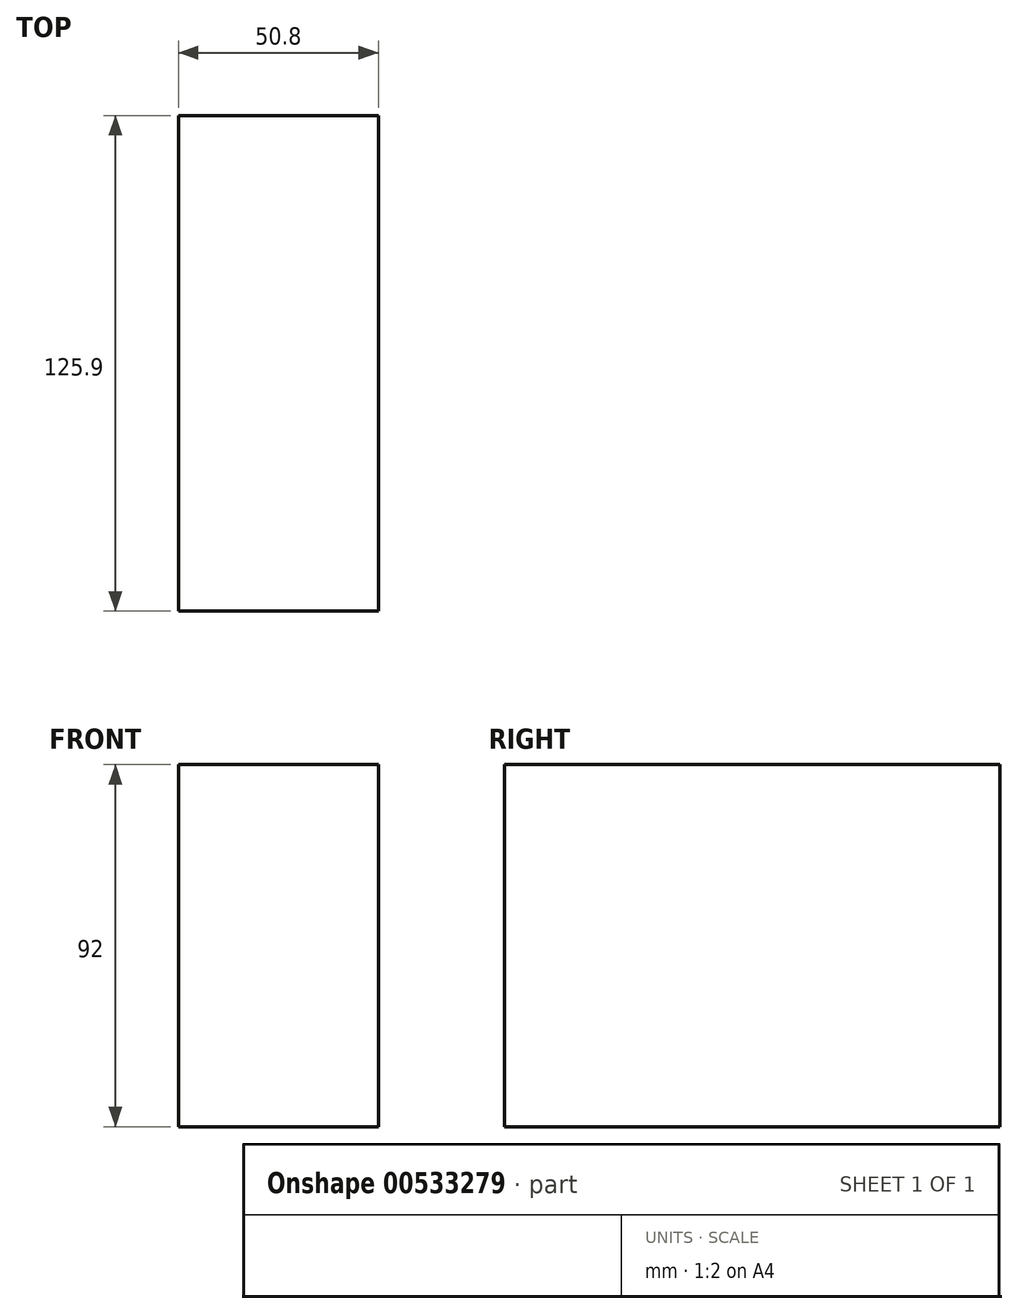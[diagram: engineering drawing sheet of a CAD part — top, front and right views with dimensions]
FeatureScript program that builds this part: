
annotation { "Feature Type Name" : "Feature", "Feature Type Description" : "" }
export const myFeature = defineFeature(function(context is Context, id is Id, definition is map)
    precondition{}
    {
        {
            var Q0;
            Q0=qCreatedBy(makeId("Right.planeOp"),FACE);
            var sketch = newSketch(context, id + "F0", { "sketchPlane" : qUnion([Q0])});
            skLineSegment(sketch, "E0.bottom", {"start": v(0, 0) * mm, "end": v(-125.9, 0) * mm});
            skLineSegment(sketch, "E0.top", {"start": v(0, -92) * mm, "end": v(-125.9, -92) * mm});
            skLineSegment(sketch, "E0.left", {"start": v(0, 0) * mm, "end": v(0, -92) * mm});
            skLineSegment(sketch, "E0.right", {"start": v(-125.9, 0) * mm, "end": v(-125.9, -92) * mm});
            skSolve(sketch);
        }
        {
            var Q0;
            Q0 = qSketchRegion(id + "F0", true);
            var Q1;
            Q1=makeQuery(id+"F0.imprint","IMPRINT",FACE,{"disambiguationData":[TD([[makeQuery(id+"F0.imprint","IMPRINT",EDGE,{"derivedFrom":sQuery(id+"F0.wireOp",EDGE,"E0.bottom")}),1.0]])]});
            extrude(context, id + "F1", {"entities" : qUnion([Q0, Q1]), "endBound" : BoundingType.SYMMETRIC, "depth" : 50.8 * mm, "offsetDistance" : 25.4 * mm});
        }
    });
